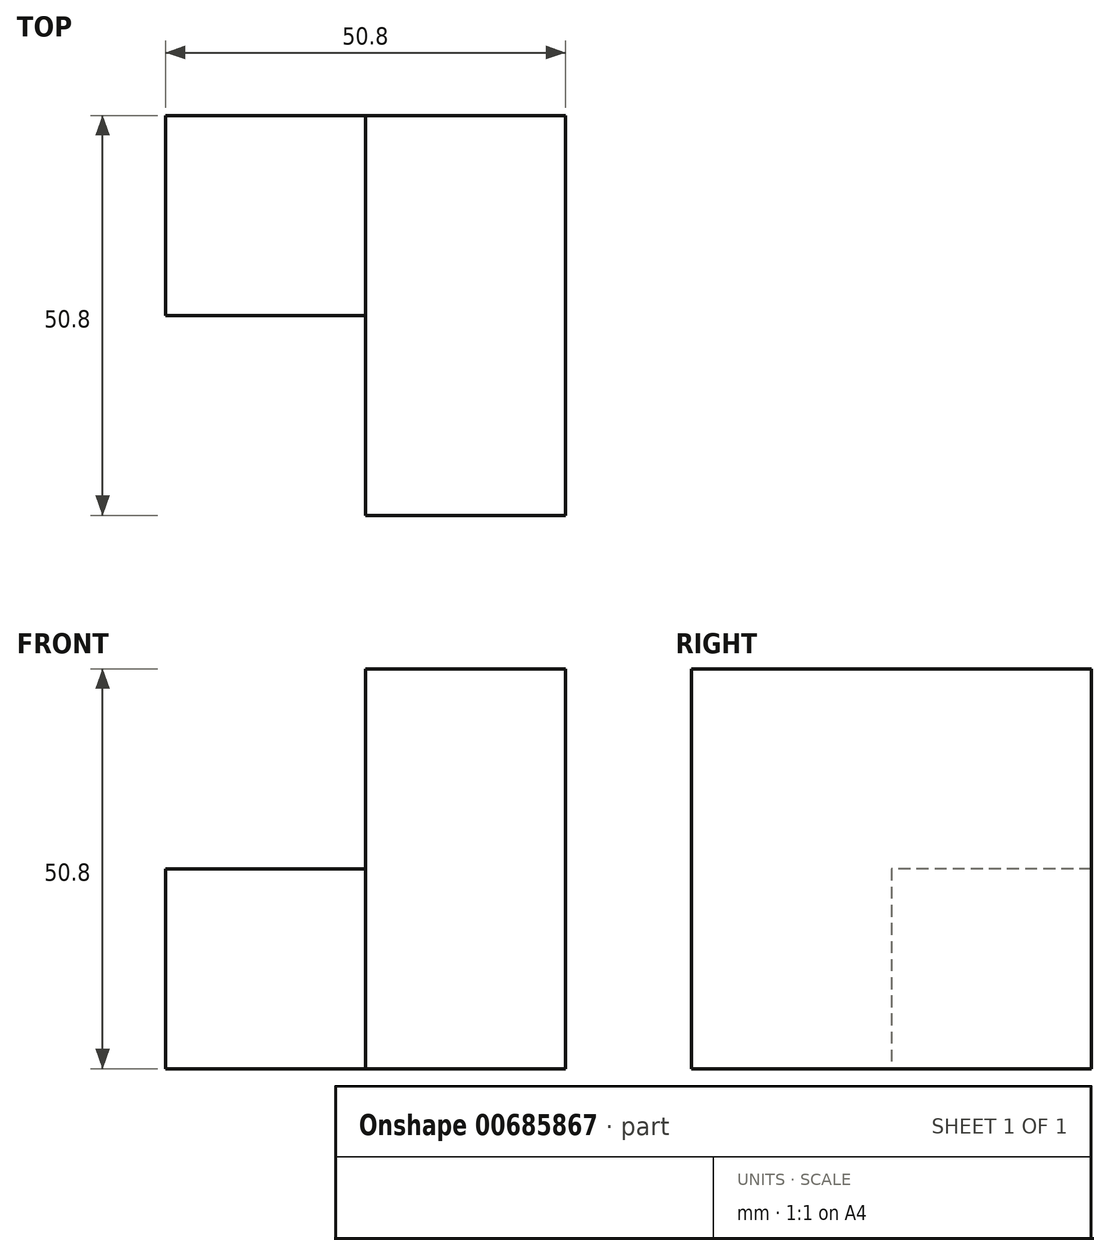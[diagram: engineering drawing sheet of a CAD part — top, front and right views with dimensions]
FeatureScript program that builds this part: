
annotation { "Feature Type Name" : "Feature", "Feature Type Description" : "" }
export const myFeature = defineFeature(function(context is Context, id is Id, definition is map)
    precondition{}
    {
        {
            var Q0;
            Q0=qCreatedBy(makeId("Front.planeOp"),FACE);
            var sketch = newSketch(context, id + "F0", { "sketchPlane" : qUnion([Q0])});
            skLineSegment(sketch, "E0.bottom", {"start": v(3.91, 11.37) * mm, "end": v(29.31, 11.37) * mm});
            skLineSegment(sketch, "E0.top", {"start": v(3.91, -39.43) * mm, "end": v(29.31, -39.43) * mm});
            skLineSegment(sketch, "E0.left", {"start": v(3.91, 11.37) * mm, "end": v(3.91, -39.43) * mm});
            skLineSegment(sketch, "E0.right", {"start": v(29.31, 11.37) * mm, "end": v(29.31, -39.43) * mm});
            skSolve(sketch);
        }
        {
            var Q0;
            Q0 = qSketchRegion(id + "F0", true);
            extrude(context, id + "F1", {"entities" : qUnion([Q0]), "depth" : 50.8 * mm, "offsetDistance" : 25.4 * mm});
        }
        {
            var Q0;
            Q0=makeQuery(id+"F1.opExtrude","SWEPT_FACE",FACE,{"disambiguationData":[OSD([sQuery(id+"F0.wireOp",EDGE,"E0.left")])]});
            var sketch = newSketch(context, id + "F2", { "sketchPlane" : qUnion([Q0])});
            skLineSegment(sketch, "E1.bottom", {"start": v(0, -14.03) * mm, "end": v(25.4, -14.03) * mm});
            skLineSegment(sketch, "E1.top", {"start": v(0, -39.43) * mm, "end": v(25.4, -39.43) * mm});
            skLineSegment(sketch, "E1.left", {"start": v(0, -14.03) * mm, "end": v(0, -39.43) * mm});
            skLineSegment(sketch, "E1.right", {"start": v(25.4, -14.03) * mm, "end": v(25.4, -39.43) * mm});
            skSolve(sketch);
        }
        {
            var Q0;
            Q0 = qSketchRegion(id + "F2", true);
            extrude(context, id + "F3", {"entities" : qUnion([Q0]), "operationType" : NewBodyOperationType.ADD, "depth" : 25.4 * mm, "offsetDistance" : 25.4 * mm});
        }
    });
